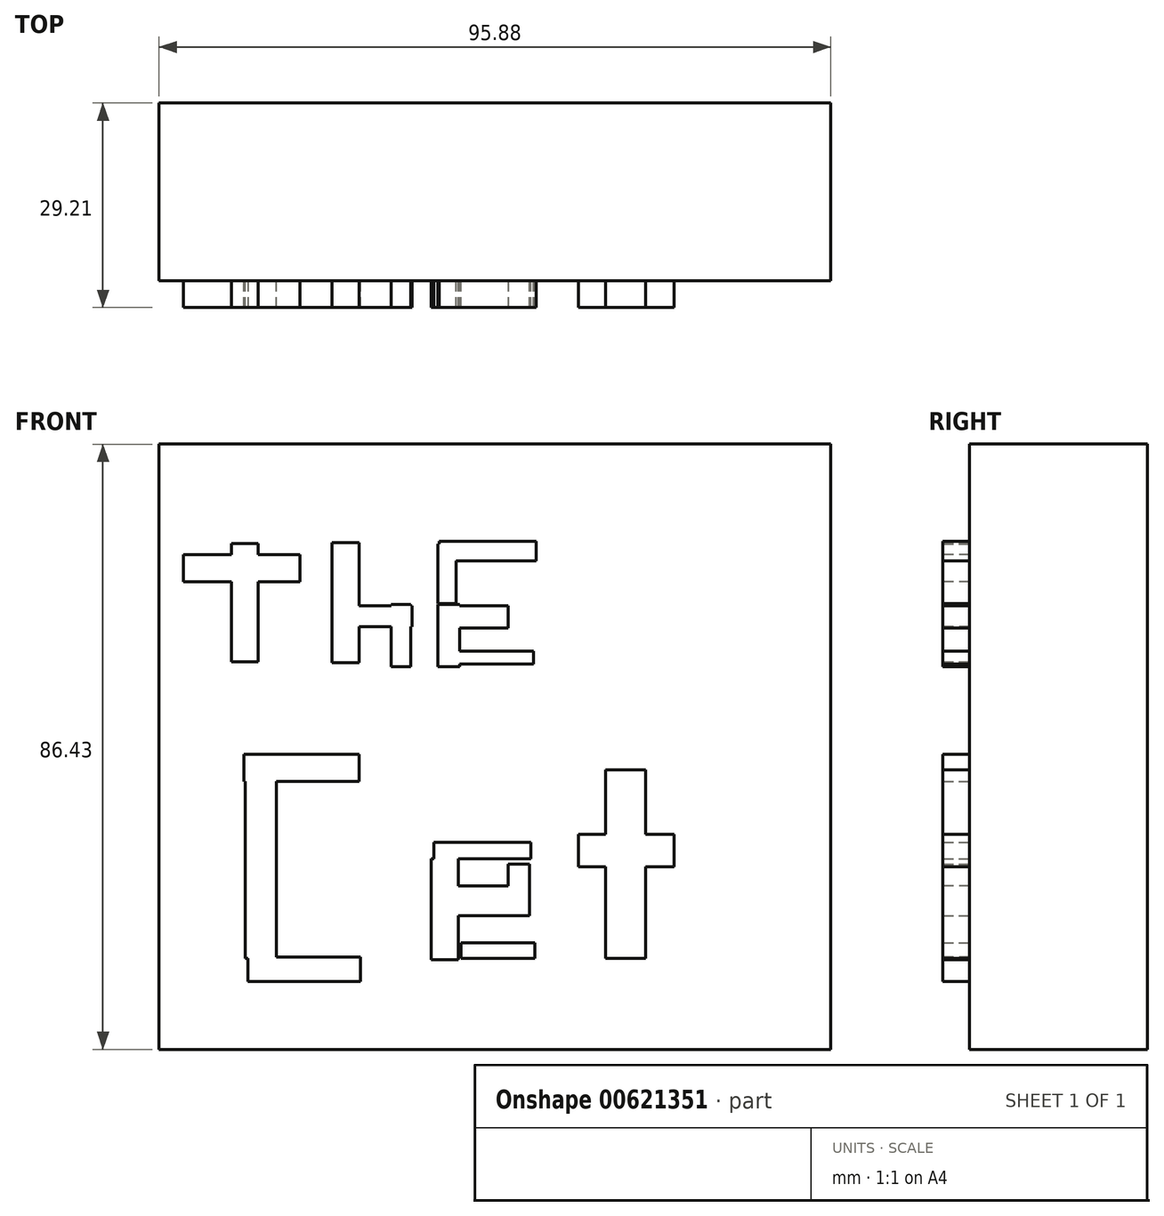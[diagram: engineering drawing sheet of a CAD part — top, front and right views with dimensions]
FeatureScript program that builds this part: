
annotation { "Feature Type Name" : "Feature", "Feature Type Description" : "" }
export const myFeature = defineFeature(function(context is Context, id is Id, definition is map)
    precondition{}
    {
        {
            var Q0;
            Q0=qCreatedBy(makeId("Front.planeOp"),FACE);
            var sketch = newSketch(context, id + "F0", { "sketchPlane" : qUnion([Q0])});
            skLineSegment(sketch, "E0.bottom", {"start": v(-49.84, 36.1) * mm, "end": v(46.04, 36.1) * mm});
            skLineSegment(sketch, "E0.top", {"start": v(-49.84, -50.33) * mm, "end": v(46.04, -50.33) * mm});
            skLineSegment(sketch, "E0.left", {"start": v(-49.84, 36.1) * mm, "end": v(-49.84, -50.33) * mm});
            skLineSegment(sketch, "E0.right", {"start": v(46.04, 36.1) * mm, "end": v(46.04, -50.33) * mm});
            skSolve(sketch);
        }
        {
            var Q0;
            Q0 = qSketchRegion(id + "F0", true);
            extrude(context, id + "F1", {"entities" : qUnion([Q0]), "depth" : 25.4 * mm, "offsetDistance" : 25.4 * mm});
        }
        {
            var Q0;
            Q0=makeQuery(id+"F1.opExtrude","CAP_FACE",FACE,{"disambiguationData":[OSD([sQuery(id+"F0.wireOp",EDGE,"E0.bottom"),sQuery(id+"F0.wireOp",EDGE,"E0.top"),sQuery(id+"F0.wireOp",EDGE,"E0.left"),sQuery(id+"F0.wireOp",EDGE,"E0.right")])],"isStart":false});
            var sketch = newSketch(context, id + "F2", { "sketchPlane" : qUnion([Q0])});
            skLineSegment(sketch, "E1.bottom", {"start": v(-39.53, 21.88) * mm, "end": v(-35.7, 21.88) * mm});
            skLineSegment(sketch, "E1.top", {"start": v(-39.53, 5) * mm, "end": v(-35.7, 5) * mm});
            skLineSegment(sketch, "E1.left", {"start": v(-39.53, 21.88) * mm, "end": v(-39.53, 5) * mm});
            skLineSegment(sketch, "E1.right", {"start": v(-35.7, 21.88) * mm, "end": v(-35.7, 5) * mm});
            skSolve(sketch);
        }
        {
            var Q0;
            Q0=makeQuery(id+"F2.imprint","IMPRINT",FACE,{"disambiguationData":[TD([[makeQuery(id+"F2.imprint","IMPRINT",EDGE,{"derivedFrom":sQuery(id+"F2.wireOp",EDGE,"E1.bottom")}),1.0]])]});
            var sketch = newSketch(context, id + "F3", { "sketchPlane" : qUnion([Q0])});
            skLineSegment(sketch, "E2.bottom", {"start": v(-46.34, 20.32) * mm, "end": v(-29.73, 20.32) * mm});
            skLineSegment(sketch, "E2.top", {"start": v(-46.34, 16.45) * mm, "end": v(-29.73, 16.45) * mm});
            skLineSegment(sketch, "E2.left", {"start": v(-46.34, 20.32) * mm, "end": v(-46.34, 16.45) * mm});
            skLineSegment(sketch, "E2.right", {"start": v(-29.73, 20.32) * mm, "end": v(-29.73, 16.45) * mm});
            skSolve(sketch);
        }
        {
            var Q0;
            Q0=makeQuery(id+"F2.imprint","IMPRINT",FACE,{"disambiguationData":[TD([[makeQuery(id+"F2.imprint","IMPRINT",EDGE,{"derivedFrom":sQuery(id+"F2.wireOp",EDGE,"E1.bottom")}),1.0]])]});
            var sketch = newSketch(context, id + "F4", { "sketchPlane" : qUnion([Q0])});
            skLineSegment(sketch, "E3.bottom", {"start": v(-25.16, 22.03) * mm, "end": v(-21.3, 22.03) * mm});
            skLineSegment(sketch, "E3.top", {"start": v(-25.16, 4.89) * mm, "end": v(-21.3, 4.89) * mm});
            skLineSegment(sketch, "E3.left", {"start": v(-25.16, 22.03) * mm, "end": v(-25.16, 4.89) * mm});
            skLineSegment(sketch, "E3.right", {"start": v(-21.3, 22.03) * mm, "end": v(-21.3, 4.89) * mm});
            skSolve(sketch);
        }
        {
            var Q0;
            Q0=makeQuery(id+"F2.imprint","IMPRINT",FACE,{"disambiguationData":[TD([[makeQuery(id+"F2.imprint","IMPRINT",EDGE,{"derivedFrom":sQuery(id+"F2.wireOp",EDGE,"E1.bottom")}),1.0]])]});
            var sketch = newSketch(context, id + "F5", { "sketchPlane" : qUnion([Q0])});
            skLineSegment(sketch, "E4.bottom", {"start": v(-25.16, 13) * mm, "end": v(-13.73, 13) * mm});
            skLineSegment(sketch, "E4.top", {"start": v(-25.16, 10.05) * mm, "end": v(-13.73, 10.05) * mm});
            skLineSegment(sketch, "E4.left", {"start": v(-25.16, 13) * mm, "end": v(-25.16, 10.05) * mm});
            skLineSegment(sketch, "E4.right", {"start": v(-13.73, 13) * mm, "end": v(-13.73, 10.05) * mm});
            skSolve(sketch);
        }
        {
            var Q0;
            Q0=makeQuery(id+"F2.imprint","IMPRINT",FACE,{"disambiguationData":[TD([[makeQuery(id+"F2.imprint","IMPRINT",EDGE,{"derivedFrom":sQuery(id+"F2.wireOp",EDGE,"E1.bottom")}),1.0]])]});
            var sketch = newSketch(context, id + "F6", { "sketchPlane" : qUnion([Q0])});
            skLineSegment(sketch, "E5.bottom", {"start": v(-13.92, 13.18) * mm, "end": v(-16.68, 13.18) * mm});
            skLineSegment(sketch, "E5.top", {"start": v(-13.92, 4.33) * mm, "end": v(-16.68, 4.33) * mm});
            skLineSegment(sketch, "E5.left", {"start": v(-13.92, 13.18) * mm, "end": v(-13.92, 4.33) * mm});
            skLineSegment(sketch, "E5.right", {"start": v(-16.68, 13.18) * mm, "end": v(-16.68, 4.33) * mm});
            skSolve(sketch);
        }
        {
            var Q0;
            Q0=makeQuery(id+"F2.imprint","IMPRINT",FACE,{"disambiguationData":[TD([[makeQuery(id+"F2.imprint","IMPRINT",EDGE,{"derivedFrom":sQuery(id+"F2.wireOp",EDGE,"E1.bottom")}),1.0]])]});
            var sketch = newSketch(context, id + "F7", { "sketchPlane" : qUnion([Q0])});
            skLineSegment(sketch, "E6.bottom", {"start": v(-10.05, 13) * mm, "end": v(0, 13) * mm});
            skLineSegment(sketch, "E6.top", {"start": v(-10.05, 9.86) * mm, "end": v(0, 9.86) * mm});
            skLineSegment(sketch, "E6.left", {"start": v(-10.05, 13) * mm, "end": v(-10.05, 9.86) * mm});
            skLineSegment(sketch, "E6.right", {"start": v(0, 13) * mm, "end": v(0, 9.86) * mm});
            skSolve(sketch);
        }
        {
            var Q0;
            Q0=makeQuery(id+"F2.imprint","IMPRINT",FACE,{"disambiguationData":[TD([[makeQuery(id+"F2.imprint","IMPRINT",EDGE,{"derivedFrom":sQuery(id+"F2.wireOp",EDGE,"E1.bottom")}),1.0]])]});
            var sketch = newSketch(context, id + "F8", { "sketchPlane" : qUnion([Q0])});
            skLineSegment(sketch, "E7.bottom", {"start": v(-10.05, 13.18) * mm, "end": v(-6.91, 13.18) * mm});
            skLineSegment(sketch, "E7.top", {"start": v(-10.05, 4.33) * mm, "end": v(-6.91, 4.33) * mm});
            skLineSegment(sketch, "E7.left", {"start": v(-10.05, 13.18) * mm, "end": v(-10.05, 4.33) * mm});
            skLineSegment(sketch, "E7.right", {"start": v(-6.91, 13.18) * mm, "end": v(-6.91, 4.33) * mm});
            skSolve(sketch);
        }
        {
            var Q0;
            Q0=makeQuery(id+"F2.imprint","IMPRINT",FACE,{"disambiguationData":[TD([[makeQuery(id+"F2.imprint","IMPRINT",EDGE,{"derivedFrom":sQuery(id+"F2.wireOp",EDGE,"E1.bottom")}),1.0]])]});
            var sketch = newSketch(context, id + "F9", { "sketchPlane" : qUnion([Q0])});
            skLineSegment(sketch, "E8.bottom", {"start": v(-9.86, 4.7) * mm, "end": v(3.6, 4.7) * mm});
            skLineSegment(sketch, "E8.top", {"start": v(-9.86, 6.54) * mm, "end": v(3.6, 6.54) * mm});
            skLineSegment(sketch, "E8.left", {"start": v(-9.86, 4.7) * mm, "end": v(-9.86, 6.54) * mm});
            skLineSegment(sketch, "E8.right", {"start": v(3.6, 4.7) * mm, "end": v(3.6, 6.54) * mm});
            skSolve(sketch);
        }
        {
            var Q0;
            Q0=makeQuery(id+"F2.imprint","IMPRINT",FACE,{"disambiguationData":[TD([[makeQuery(id+"F2.imprint","IMPRINT",EDGE,{"derivedFrom":sQuery(id+"F2.wireOp",EDGE,"E1.bottom")}),1.0]])]});
            var sketch = newSketch(context, id + "F10", { "sketchPlane" : qUnion([Q0])});
            skLineSegment(sketch, "E9.bottom", {"start": v(-10.05, 13.37) * mm, "end": v(-7.47, 13.37) * mm});
            skLineSegment(sketch, "E9.top", {"start": v(-10.05, 21.85) * mm, "end": v(-7.47, 21.85) * mm});
            skLineSegment(sketch, "E9.left", {"start": v(-10.05, 13.37) * mm, "end": v(-10.05, 21.85) * mm});
            skLineSegment(sketch, "E9.right", {"start": v(-7.47, 13.37) * mm, "end": v(-7.47, 21.85) * mm});
            skSolve(sketch);
        }
        {
            var Q0;
            Q0=makeQuery(id+"F2.imprint","IMPRINT",FACE,{"disambiguationData":[TD([[makeQuery(id+"F2.imprint","IMPRINT",EDGE,{"derivedFrom":sQuery(id+"F2.wireOp",EDGE,"E1.bottom")}),1.0]])]});
            var sketch = newSketch(context, id + "F11", { "sketchPlane" : qUnion([Q0])});
            skLineSegment(sketch, "E10.bottom", {"start": v(-9.86, 22.21) * mm, "end": v(3.96, 22.21) * mm});
            skLineSegment(sketch, "E10.top", {"start": v(-9.86, 19.45) * mm, "end": v(3.96, 19.45) * mm});
            skLineSegment(sketch, "E10.left", {"start": v(-9.86, 22.21) * mm, "end": v(-9.86, 19.45) * mm});
            skLineSegment(sketch, "E10.right", {"start": v(3.96, 22.21) * mm, "end": v(3.96, 19.45) * mm});
            skSolve(sketch);
        }
        {
            var Q0;
            Q0=makeQuery(id+"F2.imprint","IMPRINT",FACE,{"disambiguationData":[TD([[makeQuery(id+"F2.imprint","IMPRINT",EDGE,{"derivedFrom":sQuery(id+"F2.wireOp",EDGE,"E1.bottom")}),1.0]])]});
            var sketch = newSketch(context, id + "F12", { "sketchPlane" : qUnion([Q0])});
            skLineSegment(sketch, "E11.bottom", {"start": v(-37.52, -37.33) * mm, "end": v(-33.1, -37.33) * mm});
            skLineSegment(sketch, "E11.top", {"start": v(-37.52, -8.2) * mm, "end": v(-33.1, -8.2) * mm});
            skLineSegment(sketch, "E11.left", {"start": v(-37.52, -37.33) * mm, "end": v(-37.52, -8.2) * mm});
            skLineSegment(sketch, "E11.right", {"start": v(-33.1, -37.33) * mm, "end": v(-33.1, -8.2) * mm});
            skSolve(sketch);
        }
        {
            var Q0;
            Q0=makeQuery(id+"F2.imprint","IMPRINT",FACE,{"disambiguationData":[TD([[makeQuery(id+"F2.imprint","IMPRINT",EDGE,{"derivedFrom":sQuery(id+"F2.wireOp",EDGE,"E1.bottom")}),1.0]])]});
            var sketch = newSketch(context, id + "F13", { "sketchPlane" : qUnion([Q0])});
            skLineSegment(sketch, "E12.bottom", {"start": v(-37.7, -8.2) * mm, "end": v(-21.3, -8.2) * mm});
            skLineSegment(sketch, "E12.top", {"start": v(-37.7, -12.08) * mm, "end": v(-21.3, -12.08) * mm});
            skLineSegment(sketch, "E12.left", {"start": v(-37.7, -8.2) * mm, "end": v(-37.7, -12.08) * mm});
            skLineSegment(sketch, "E12.right", {"start": v(-21.3, -8.2) * mm, "end": v(-21.3, -12.08) * mm});
            skSolve(sketch);
        }
        {
            var Q0;
            Q0=makeQuery(id+"F2.imprint","IMPRINT",FACE,{"disambiguationData":[TD([[makeQuery(id+"F2.imprint","IMPRINT",EDGE,{"derivedFrom":sQuery(id+"F2.wireOp",EDGE,"E1.bottom")}),1.0]])]});
            var sketch = newSketch(context, id + "F14", { "sketchPlane" : qUnion([Q0])});
            skLineSegment(sketch, "E13.bottom", {"start": v(-37.15, -37.15) * mm, "end": v(-21.1, -37.15) * mm});
            skLineSegment(sketch, "E13.top", {"start": v(-37.15, -40.65) * mm, "end": v(-21.1, -40.65) * mm});
            skLineSegment(sketch, "E13.left", {"start": v(-37.15, -37.15) * mm, "end": v(-37.15, -40.65) * mm});
            skLineSegment(sketch, "E13.right", {"start": v(-21.1, -37.15) * mm, "end": v(-21.1, -40.65) * mm});
            skSolve(sketch);
        }
        {
            var Q0;
            Q0=makeQuery(id+"F13.imprint","IMPRINT",FACE,{"disambiguationData":[TD([[makeQuery(id+"F13.imprint","IMPRINT",EDGE,{"derivedFrom":sQuery(id+"F13.wireOp",EDGE,"E12.bottom")}),1.0]])]});
            var sketch = newSketch(context, id + "F15", { "sketchPlane" : qUnion([Q0])});
            skLineSegment(sketch, "E14.bottom", {"start": v(-10.97, -37.52) * mm, "end": v(-7.1, -37.52) * mm});
            skLineSegment(sketch, "E14.top", {"start": v(-10.97, -23.14) * mm, "end": v(-7.1, -23.14) * mm});
            skLineSegment(sketch, "E14.left", {"start": v(-10.97, -37.52) * mm, "end": v(-10.97, -23.14) * mm});
            skLineSegment(sketch, "E14.right", {"start": v(-7.1, -37.52) * mm, "end": v(-7.1, -23.14) * mm});
            skSolve(sketch);
        }
        {
            var Q0;
            Q0=makeQuery(id+"F6.imprint","IMPRINT",FACE,{"disambiguationData":[TD([[makeQuery(id+"F6.imprint","IMPRINT",EDGE,{"derivedFrom":sQuery(id+"F6.wireOp",EDGE,"E5.bottom")}),-1.0]])]});
            var sketch = newSketch(context, id + "F16", { "sketchPlane" : qUnion([Q0])});
            skLineSegment(sketch, "E15.bottom", {"start": v(-10.6, -23.14) * mm, "end": v(3.23, -23.14) * mm});
            skLineSegment(sketch, "E15.top", {"start": v(-10.6, -20.74) * mm, "end": v(3.23, -20.74) * mm});
            skLineSegment(sketch, "E15.left", {"start": v(-10.6, -23.14) * mm, "end": v(-10.6, -20.74) * mm});
            skLineSegment(sketch, "E15.right", {"start": v(3.23, -23.14) * mm, "end": v(3.23, -20.74) * mm});
            skSolve(sketch);
        }
        {
            var Q0;
            Q0=makeQuery(id+"F6.imprint","IMPRINT",FACE,{"disambiguationData":[TD([[makeQuery(id+"F6.imprint","IMPRINT",EDGE,{"derivedFrom":sQuery(id+"F6.wireOp",EDGE,"E5.bottom")}),-1.0]])]});
            var sketch = newSketch(context, id + "F17", { "sketchPlane" : qUnion([Q0])});
            skLineSegment(sketch, "E16.bottom", {"start": v(3.04, -23.87) * mm, "end": v(0, -23.87) * mm});
            skLineSegment(sketch, "E16.top", {"start": v(3.04, -27.38) * mm, "end": v(0, -27.38) * mm});
            skLineSegment(sketch, "E16.left", {"start": v(3.04, -23.87) * mm, "end": v(3.04, -27.38) * mm});
            skLineSegment(sketch, "E16.right", {"start": v(0, -23.87) * mm, "end": v(0, -27.38) * mm});
            skSolve(sketch);
        }
        {
            var Q0;
            Q0=makeQuery(id+"F6.imprint","IMPRINT",FACE,{"disambiguationData":[TD([[makeQuery(id+"F6.imprint","IMPRINT",EDGE,{"derivedFrom":sQuery(id+"F6.wireOp",EDGE,"E5.bottom")}),-1.0]])]});
            var sketch = newSketch(context, id + "F18", { "sketchPlane" : qUnion([Q0])});
            skLineSegment(sketch, "E17.bottom", {"start": v(3.04, -27) * mm, "end": v(-7.1, -27) * mm});
            skLineSegment(sketch, "E17.top", {"start": v(3.04, -31.25) * mm, "end": v(-7.1, -31.25) * mm});
            skLineSegment(sketch, "E17.left", {"start": v(3.04, -27) * mm, "end": v(3.04, -31.25) * mm});
            skLineSegment(sketch, "E17.right", {"start": v(-7.1, -27) * mm, "end": v(-7.1, -31.25) * mm});
            skSolve(sketch);
        }
        {
            var Q0;
            Q0=makeQuery(id+"F6.imprint","IMPRINT",FACE,{"disambiguationData":[TD([[makeQuery(id+"F6.imprint","IMPRINT",EDGE,{"derivedFrom":sQuery(id+"F6.wireOp",EDGE,"E5.bottom")}),-1.0]])]});
            var sketch = newSketch(context, id + "F19", { "sketchPlane" : qUnion([Q0])});
            skLineSegment(sketch, "E18.bottom", {"start": v(-6.73, -37.33) * mm, "end": v(3.78, -37.33) * mm});
            skLineSegment(sketch, "E18.top", {"start": v(-6.73, -35.12) * mm, "end": v(3.78, -35.12) * mm});
            skLineSegment(sketch, "E18.left", {"start": v(-6.73, -37.33) * mm, "end": v(-6.73, -35.12) * mm});
            skLineSegment(sketch, "E18.right", {"start": v(3.78, -37.33) * mm, "end": v(3.78, -35.12) * mm});
            skSolve(sketch);
        }
        {
            var Q0;
            Q0=makeQuery(id+"F6.imprint","IMPRINT",FACE,{"disambiguationData":[TD([[makeQuery(id+"F6.imprint","IMPRINT",EDGE,{"derivedFrom":sQuery(id+"F6.wireOp",EDGE,"E5.bottom")}),-1.0]])]});
            var sketch = newSketch(context, id + "F20", { "sketchPlane" : qUnion([Q0])});
            skLineSegment(sketch, "E19.bottom", {"start": v(19.63, -10.42) * mm, "end": v(13.92, -10.42) * mm});
            skLineSegment(sketch, "E19.top", {"start": v(19.63, -37.33) * mm, "end": v(13.92, -37.33) * mm});
            skLineSegment(sketch, "E19.left", {"start": v(19.63, -10.42) * mm, "end": v(19.63, -37.33) * mm});
            skLineSegment(sketch, "E19.right", {"start": v(13.92, -10.42) * mm, "end": v(13.92, -37.33) * mm});
            skSolve(sketch);
        }
        {
            var Q0;
            Q0=makeQuery(id+"F6.imprint","IMPRINT",FACE,{"disambiguationData":[TD([[makeQuery(id+"F6.imprint","IMPRINT",EDGE,{"derivedFrom":sQuery(id+"F6.wireOp",EDGE,"E5.bottom")}),-1.0]])]});
            var sketch = newSketch(context, id + "F21", { "sketchPlane" : qUnion([Q0])});
            skLineSegment(sketch, "E20.bottom", {"start": v(10.05, -19.63) * mm, "end": v(23.69, -19.63) * mm});
            skLineSegment(sketch, "E20.top", {"start": v(10.05, -24.24) * mm, "end": v(23.69, -24.24) * mm});
            skLineSegment(sketch, "E20.left", {"start": v(10.05, -19.63) * mm, "end": v(10.05, -24.24) * mm});
            skLineSegment(sketch, "E20.right", {"start": v(23.69, -19.63) * mm, "end": v(23.69, -24.24) * mm});
            skSolve(sketch);
        }
        {
            var Q0;
            Q0=makeQuery(id+"F2.imprint","IMPRINT",FACE,{"disambiguationData":[TD([[makeQuery(id+"F2.imprint","IMPRINT",EDGE,{"derivedFrom":sQuery(id+"F2.wireOp",EDGE,"E1.bottom")}),-1.0]])]});
            extrude(context, id + "F22", {"entities" : qUnion([Q0]), "operationType" : NewBodyOperationType.ADD, "depth" : 3.8 * mm, "offsetDistance" : 25.4 * mm});
        }
        {
            var Q0;
            Q0 = qSketchRegion(id + "F4", true);
            extrude(context, id + "F23", {"entities" : qUnion([Q0]), "operationType" : NewBodyOperationType.ADD, "depth" : 3.8 * mm, "offsetDistance" : 25.4 * mm});
        }
        {
            var Q0;
            Q0 = qSketchRegion(id + "F6", true);
            extrude(context, id + "F24", {"entities" : qUnion([Q0]), "operationType" : NewBodyOperationType.ADD, "depth" : 3.8 * mm, "offsetDistance" : 25.4 * mm});
        }
        {
            var Q0;
            Q0 = qSketchRegion(id + "F3", true);
            extrude(context, id + "F25", {"entities" : qUnion([Q0]), "operationType" : NewBodyOperationType.ADD, "depth" : 3.8 * mm, "offsetDistance" : 25.4 * mm});
        }
        {
            var Q0;
            Q0 = qSketchRegion(id + "F5", true);
            extrude(context, id + "F26", {"entities" : qUnion([Q0]), "operationType" : NewBodyOperationType.ADD, "depth" : 3.8 * mm, "offsetDistance" : 25.4 * mm});
        }
        {
            var Q0;
            Q0 = qSketchRegion(id + "F7", true);
            extrude(context, id + "F27", {"entities" : qUnion([Q0]), "operationType" : NewBodyOperationType.ADD, "depth" : 3.8 * mm, "offsetDistance" : 25.4 * mm});
        }
        {
            var Q0;
            Q0 = qSketchRegion(id + "F21", true);
            extrude(context, id + "F28", {"entities" : qUnion([Q0]), "operationType" : NewBodyOperationType.ADD, "depth" : 3.8 * mm, "offsetDistance" : 25.4 * mm});
        }
        {
            var Q0;
            Q0 = qSketchRegion(id + "F20", true);
            extrude(context, id + "F29", {"entities" : qUnion([Q0]), "operationType" : NewBodyOperationType.ADD, "depth" : 3.8 * mm, "offsetDistance" : 25.4 * mm});
        }
        {
            var Q0;
            Q0 = qSketchRegion(id + "F19", true);
            extrude(context, id + "F30", {"entities" : qUnion([Q0]), "operationType" : NewBodyOperationType.ADD, "depth" : 3.8 * mm, "offsetDistance" : 25.4 * mm});
        }
        {
            var Q0;
            Q0 = qSketchRegion(id + "F18", true);
            extrude(context, id + "F31", {"entities" : qUnion([Q0]), "operationType" : NewBodyOperationType.ADD, "depth" : 3.8 * mm, "offsetDistance" : 25.4 * mm});
        }
        {
            var Q0;
            Q0 = qSketchRegion(id + "F17", true);
            extrude(context, id + "F32", {"entities" : qUnion([Q0]), "operationType" : NewBodyOperationType.ADD, "depth" : 3.8 * mm, "offsetDistance" : 25.4 * mm});
        }
        {
            var Q0;
            Q0 = qSketchRegion(id + "F16", true);
            extrude(context, id + "F33", {"entities" : qUnion([Q0]), "operationType" : NewBodyOperationType.ADD, "depth" : 3.8 * mm, "offsetDistance" : 25.4 * mm});
        }
        {
            var Q0;
            Q0 = qSketchRegion(id + "F15", true);
            extrude(context, id + "F34", {"entities" : qUnion([Q0]), "operationType" : NewBodyOperationType.ADD, "depth" : 3.8 * mm, "offsetDistance" : 25.4 * mm});
        }
        {
            var Q0;
            Q0 = qSketchRegion(id + "F14", true);
            extrude(context, id + "F35", {"entities" : qUnion([Q0]), "operationType" : NewBodyOperationType.ADD, "depth" : 3.8 * mm, "offsetDistance" : 25.4 * mm});
        }
        {
            var Q0;
            Q0 = qSketchRegion(id + "F8", true);
            extrude(context, id + "F36", {"entities" : qUnion([Q0]), "operationType" : NewBodyOperationType.ADD, "depth" : 3.8 * mm, "offsetDistance" : 25.4 * mm});
        }
        {
            var Q0;
            Q0 = qSketchRegion(id + "F9", true);
            extrude(context, id + "F37", {"entities" : qUnion([Q0]), "operationType" : NewBodyOperationType.ADD, "depth" : 3.8 * mm, "offsetDistance" : 25.4 * mm});
        }
        {
            var Q0;
            Q0 = qSketchRegion(id + "F10", true);
            extrude(context, id + "F38", {"entities" : qUnion([Q0]), "operationType" : NewBodyOperationType.ADD, "depth" : 3.8 * mm, "offsetDistance" : 25.4 * mm});
        }
        {
            var Q0;
            Q0 = qSketchRegion(id + "F11", true);
            extrude(context, id + "F39", {"entities" : qUnion([Q0]), "operationType" : NewBodyOperationType.ADD, "depth" : 3.8 * mm, "offsetDistance" : 25.4 * mm});
        }
        {
            var Q0;
            Q0 = qSketchRegion(id + "F12", true);
            extrude(context, id + "F40", {"entities" : qUnion([Q0]), "operationType" : NewBodyOperationType.ADD, "depth" : 3.8 * mm, "offsetDistance" : 25.4 * mm});
        }
        {
            var Q0;
            Q0 = qSketchRegion(id + "F13", true);
            extrude(context, id + "F41", {"entities" : qUnion([Q0]), "operationType" : NewBodyOperationType.ADD, "depth" : 3.8 * mm, "offsetDistance" : 25.4 * mm});
        }
    });
